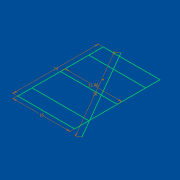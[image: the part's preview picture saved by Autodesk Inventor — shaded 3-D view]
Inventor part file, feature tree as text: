
AUTODESK INVENTOR PART (.ipt)
format: ipt  version: 2016 (Build 200138000, 138)  size: 63,488 bytes
history: native  units: mm
features: sketch x1
ambient origin geometry x8: Origin, YZ Plane, XZ Plane, XY Plane, X Axis, Y Axis, Z Axis, Center Point
feature tree (1):
  sketch  "Sketch1"  dims[d0=24.0mm d1=16.0mm d2=15.96mm d3=30.0mm]
